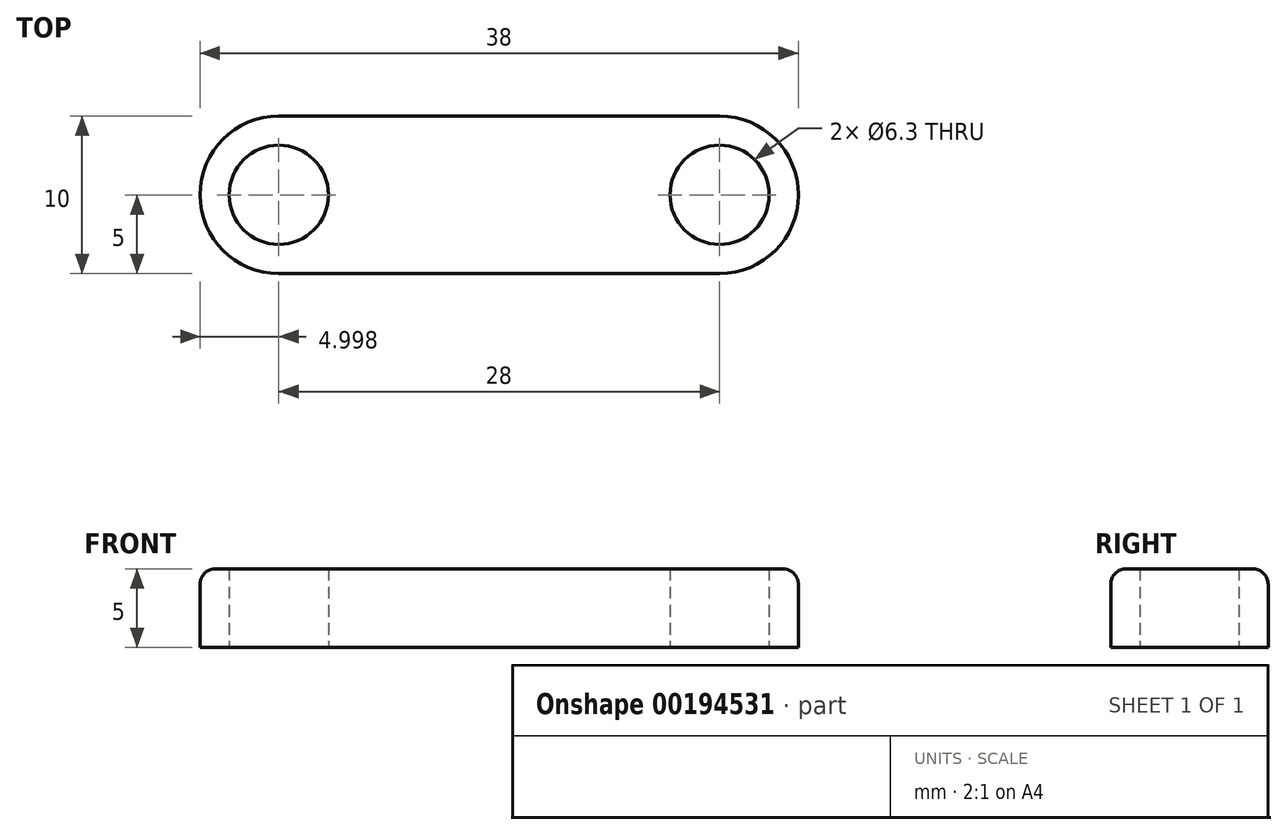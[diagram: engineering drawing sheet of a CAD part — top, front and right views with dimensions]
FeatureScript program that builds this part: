
annotation { "Feature Type Name" : "Feature", "Feature Type Description" : "" }
export const myFeature = defineFeature(function(context is Context, id is Id, definition is map)
    precondition{}
    {
        {
            var Q0;
            Q0=qCreatedBy(makeId("Top.planeOp"),FACE);
            var sketch = newSketch(context, id + "F0", { "sketchPlane" : qUnion([Q0])});
            skLineSegment(sketch, "E0", {"start": v(-54.81, 43.85) * mm, "end": v(-54.81, 33.85) * mm});
            skLineSegment(sketch, "E1", {"start": v(-54.81, 33.85) * mm, "end": v(-16.81, 33.85) * mm});
            skLineSegment(sketch, "E2", {"start": v(-16.81, 33.85) * mm, "end": v(-16.81, 43.85) * mm});
            skLineSegment(sketch, "E3", {"start": v(-54.81, 43.85) * mm, "end": v(-16.81, 43.85) * mm});
            skLineSegment(sketch, "E4", {"start": v(-54.81, 43.85) * mm, "end": v(-49.81, 43.85) * mm});
            skCircle(sketch, "E5", {"center": v(-49.81, 38.85) * mm, "radius": 3.15 * mm});
            skCircle(sketch, "E6", {"center": v(-21.81, 38.85) * mm, "radius": 3.15 * mm});
            skSolve(sketch);
        }
        {
            var Q0;
            Q0 = qSketchRegion(id + "F0", true);
            var Q1;
            Q1=makeQuery(id+"F0.imprint","IMPRINT",FACE,{"disambiguationData":[TD([[makeQuery(id+"F0.imprint","IMPRINT",EDGE,{"derivedFrom":sQuery(id+"F0.wireOp",EDGE,"E0")}),1.0]])]});
            extrude(context, id + "F1", {"entities" : qUnion([Q0, Q1]), "depth" : 5 * mm});
        }
        {
            var Q0;
            Q0=makeQuery(id+"F1.opExtrude","SWEPT_EDGE",EDGE,{"disambiguationData":[OSD([sQuery(id+"F0.wireOp",EDGE,"E0"),sQuery(id+"F0.wireOp",EDGE,"E1")])]});
            var Q1;
            Q1=makeQuery(id+"F1.opExtrude","SWEPT_EDGE",EDGE,{"disambiguationData":[OSD([sQuery(id+"F0.wireOp",EDGE,"E0"),sQuery(id+"F0.wireOp",EDGE,"E4")])]});
            var Q2;
            Q2=makeQuery(id+"F1.opExtrude","SWEPT_EDGE",EDGE,{"disambiguationData":[OSD([sQuery(id+"F0.wireOp",EDGE,"E2"),sQuery(id+"F0.wireOp",EDGE,"E3")])]});
            var Q3;
            Q3=makeQuery(id+"F1.opExtrude","SWEPT_EDGE",EDGE,{"disambiguationData":[OSD([sQuery(id+"F0.wireOp",EDGE,"E1"),sQuery(id+"F0.wireOp",EDGE,"E2")])]});
            fillet(context, id + "F2", {"entities" : qUnion([Q0, Q1, Q2, Q3]), "radius" : 5 * mm, "tangentPropagation" : true, "allowEdgeOverflow" : false});
        }
        {
            var Q0;
            Q0=makeQuery(id+"F1.opExtrude","CAP_EDGE",EDGE,{"disambiguationData":[OSD([sQuery(id+"F0.wireOp",EDGE,"E1")])],"isStart":false});
            var Q1;
            Q1=makeQuery(id+"F1.opExtrude","CAP_EDGE",EDGE,{"disambiguationData":[OSD([sQuery(id+"F0.wireOp",EDGE,"E3"),sQuery(id+"F0.wireOp",EDGE,"E4")])],"isStart":false});
            fillet(context, id + "F3", {"entities" : qUnion([Q0, Q1]), "radius" : 1 * mm, "tangentPropagation" : true, "allowEdgeOverflow" : false});
        }
    });
